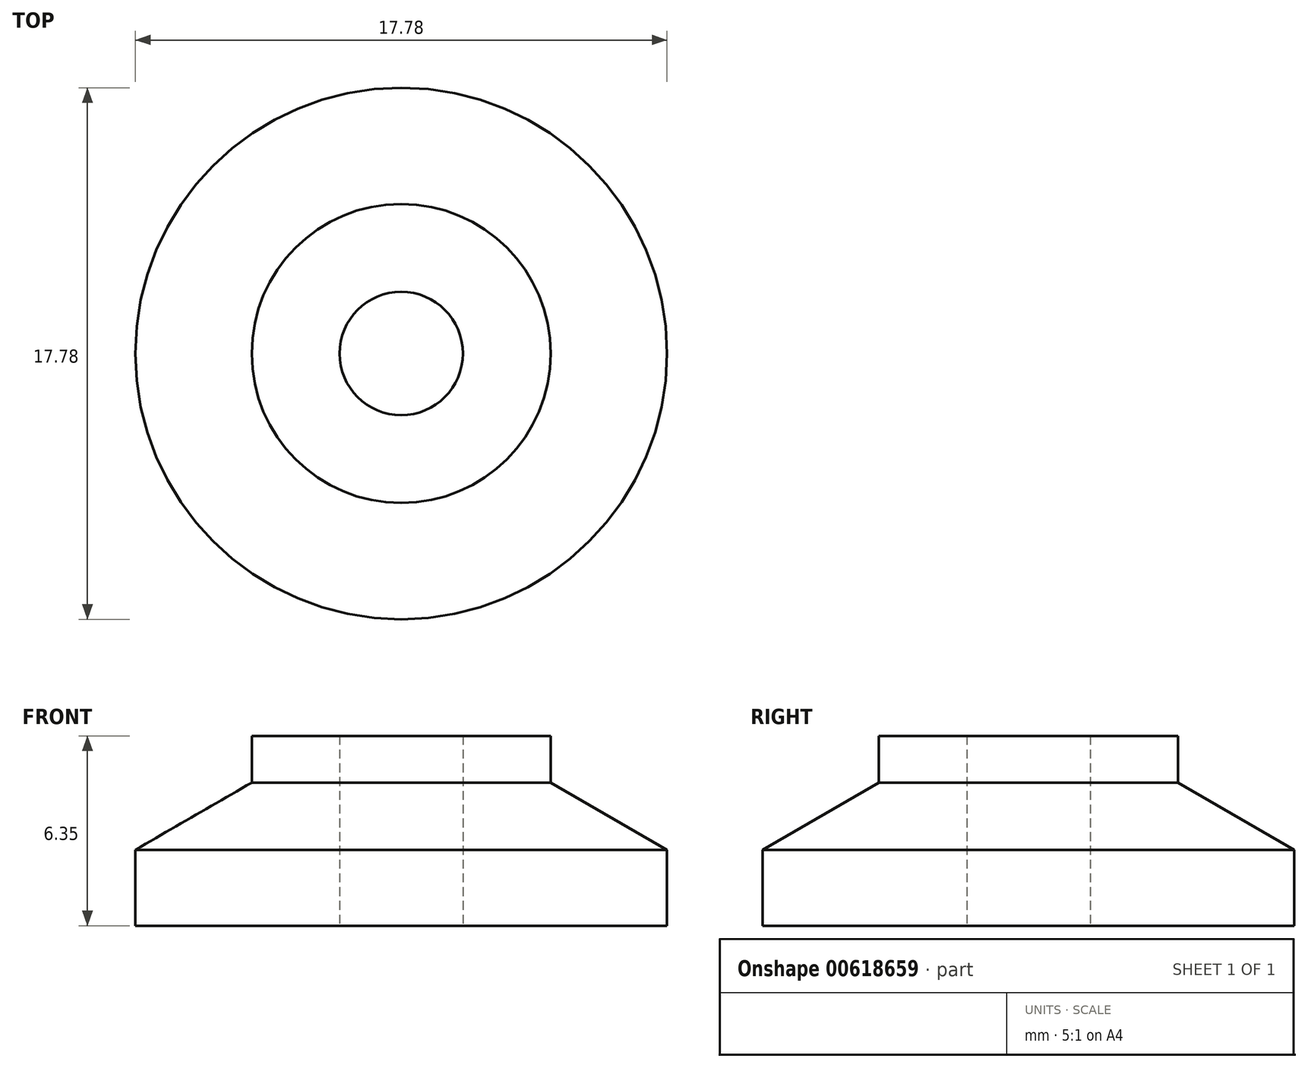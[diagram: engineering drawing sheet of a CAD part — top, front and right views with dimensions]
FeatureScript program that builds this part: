
annotation { "Feature Type Name" : "Feature", "Feature Type Description" : "" }
export const myFeature = defineFeature(function(context is Context, id is Id, definition is map)
    precondition{}
    {
        {
            var Q0;
            Q0=qCreatedBy(makeId("Front.planeOp"),FACE);
            var sketch = newSketch(context, id + "F0", { "sketchPlane" : qUnion([Q0])});
            skLineSegment(sketch, "E0", {"start": v(0, 0) * mm, "end": v(0, 6.35) * mm, "construction": true});
            skLineSegment(sketch, "E1.bottom", {"start": v(2.06, 0) * mm, "end": v(5, 0) * mm});
            skLineSegment(sketch, "E1.top", {"start": v(2.06, 6.35) * mm, "end": v(5, 6.35) * mm});
            skLineSegment(sketch, "E1.left", {"start": v(2.06, 0) * mm, "end": v(2.06, 6.35) * mm});
            skLineSegment(sketch, "E1.right", {"start": v(5, 0) * mm, "end": v(5, 6.35) * mm});
            skLineSegment(sketch, "E2", {"start": v(5, 0) * mm, "end": v(8.9, 0) * mm});
            skLineSegment(sketch, "E3", {"start": v(8.9, 0) * mm, "end": v(8.9, 2.54) * mm});
            skLineSegment(sketch, "E4", {"start": v(8.9, 2.54) * mm, "end": v(5, 4.79) * mm});
            skSolve(sketch);
        }
        {
            var Q0;
            Q0 = qSketchRegion(id + "F0", true);
            var Q1;
            Q1=sQuery(id+"F0.wireOp",EDGE,"E0");
            revolve(context, id + "F1", {"entities" : qUnion([Q0]), "axis" : qUnion([Q1]), "revolveType" : RevolveType.FULL});
        }
    });
